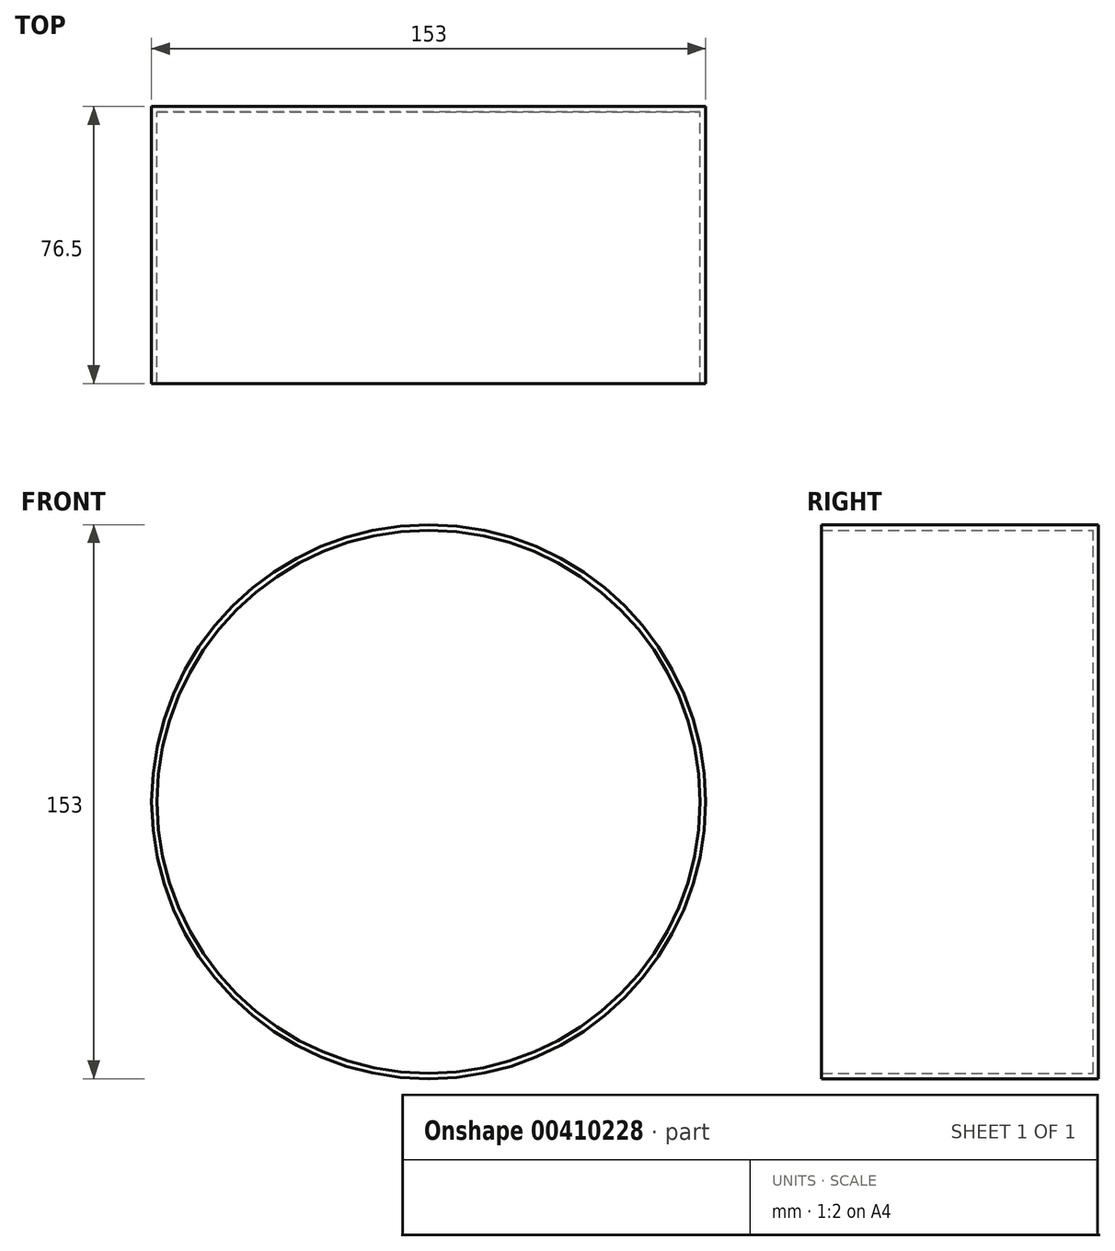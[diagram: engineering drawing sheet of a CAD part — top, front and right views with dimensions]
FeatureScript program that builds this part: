
annotation { "Feature Type Name" : "Feature", "Feature Type Description" : "" }
export const myFeature = defineFeature(function(context is Context, id is Id, definition is map)
    precondition{}
    {
        {
            var Q0;
            Q0=qCreatedBy(makeId("Front.planeOp"),FACE);
            var sketch = newSketch(context, id + "F0", { "sketchPlane" : qUnion([Q0])});
            skCircle(sketch, "E0", {"center": v(0, 0) * mm, "radius": 75 * mm});
            skSolve(sketch);
        }
        {
            var Q0;
            Q0=makeQuery(id+"F0.imprint","IMPRINT",FACE,{"disambiguationData":[TD([[makeQuery(id+"F0.imprint","IMPRINT",EDGE,{"derivedFrom":sQuery(id+"F0.wireOp",EDGE,"E0")}),1.0]])]});
            extrude(context, id + "F1", {"entities" : qUnion([Q0]), "depth" : 75 * mm});
        }
        {
            var Q0;
            Q0=makeQuery(id+"F1.opExtrude","CAP_FACE",FACE,{"disambiguationData":[OSD([sQuery(id+"F0.wireOp",EDGE,"E0")])],"isStart":false});
            shell(context, id + "F2", {"entities" : qUnion([Q0]), "thickness" : 1.5 * mm, "oppositeDirection" : true});
        }
    });
